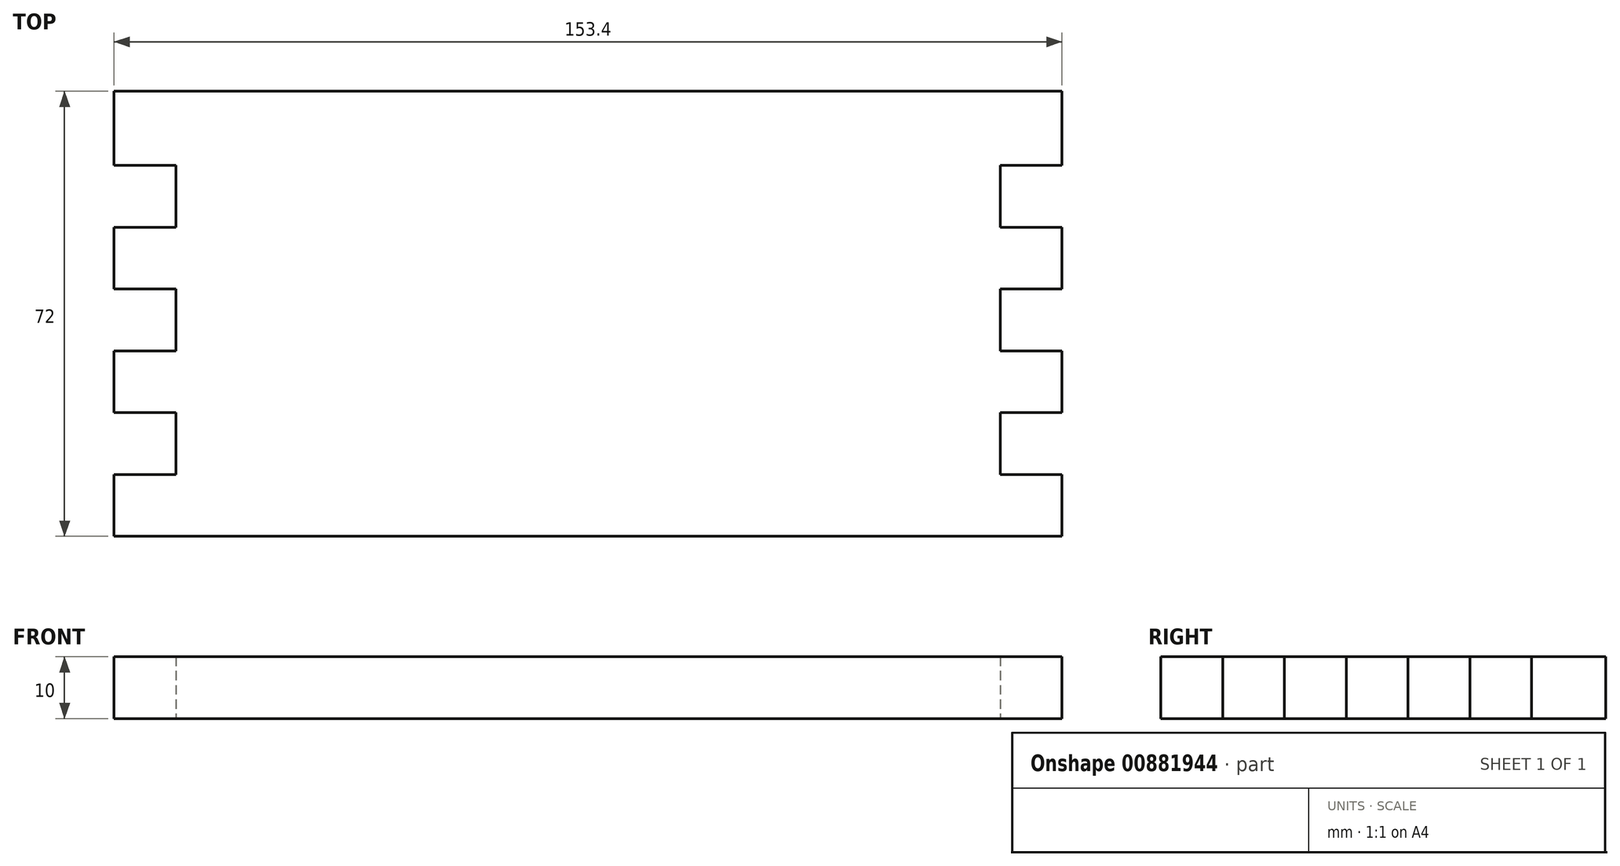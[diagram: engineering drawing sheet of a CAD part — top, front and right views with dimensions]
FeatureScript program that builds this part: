
annotation { "Feature Type Name" : "Feature", "Feature Type Description" : "" }
export const myFeature = defineFeature(function(context is Context, id is Id, definition is map)
    precondition{}
    {
        {
            var Q0;
            Q0=qCreatedBy(makeId("Top.planeOp"),FACE);
            var sketch = newSketch(context, id + "F0", { "sketchPlane" : qUnion([Q0])});
            skLineSegment(sketch, "E0.bottom", {"start": v(-145.63, 36.94) * mm, "end": v(7.77, 36.94) * mm});
            skLineSegment(sketch, "E0.top", {"start": v(-145.63, -33.06) * mm, "end": v(7.77, -33.06) * mm});
            skLineSegment(sketch, "E0.left", {"start": v(-145.63, 36.94) * mm, "end": v(-145.63, -33.06) * mm});
            skLineSegment(sketch, "E0.right", {"start": v(7.77, 36.94) * mm, "end": v(7.77, -33.06) * mm});
            skLineSegment(sketch, "E1.bottom", {"start": v(-145.63, 36.94) * mm, "end": v(-135.63, 36.94) * mm});
            skLineSegment(sketch, "E1.top", {"start": v(-145.63, -33.06) * mm, "end": v(-135.63, -33.06) * mm});
            skLineSegment(sketch, "E1.right", {"start": v(-135.63, 36.94) * mm, "end": v(-135.63, -33.06) * mm});
            skLineSegment(sketch, "E2.bottom", {"start": v(7.77, 36.94) * mm, "end": v(-2.23, 36.94) * mm});
            skLineSegment(sketch, "E2.top", {"start": v(7.77, -33.06) * mm, "end": v(-2.23, -33.06) * mm});
            skLineSegment(sketch, "E2.right", {"start": v(-2.23, 36.94) * mm, "end": v(-2.23, -33.06) * mm});
            skLineSegment(sketch, "E3.left", {"start": v(-145.63, 36.94) * mm, "end": v(-145.63, 26.94) * mm});
            skLineSegment(sketch, "E4.bottom", {"start": v(-2.23, 36.94) * mm, "end": v(7.77, 36.94) * mm});
            skLineSegment(sketch, "E4.top", {"start": v(-2.23, 26.94) * mm, "end": v(7.77, 26.94) * mm});
            skLineSegment(sketch, "E4.left", {"start": v(-2.23, 36.94) * mm, "end": v(-2.23, 26.94) * mm});
            skLineSegment(sketch, "E4.right", {"start": v(7.77, 36.94) * mm, "end": v(7.77, 26.94) * mm});
            skLineSegment(sketch, "E5.MirrorCS", {"start": v(7.77, 16.94) * mm, "end": v(-2.23, 16.94) * mm});
            skLineSegment(sketch, "E6.MirrorCS", {"start": v(-2.23, 6.94) * mm, "end": v(7.77, 6.94) * mm});
            skLineSegment(sketch, "E7.MirrorCS", {"start": v(7.77, -3.06) * mm, "end": v(-2.23, -3.06) * mm});
            skLineSegment(sketch, "E8.MirrorCS", {"start": v(-2.23, -13.06) * mm, "end": v(7.77, -13.06) * mm});
            skLineSegment(sketch, "E9.MirrorCS", {"start": v(7.77, -23.06) * mm, "end": v(-2.23, -23.06) * mm});
            skLineSegment(sketch, "E10.MirrorCS", {"start": v(-2.23, -33.06) * mm, "end": v(7.77, -33.06) * mm});
            skLineSegment(sketch, "E11.top", {"start": v(-145.63, 26.94) * mm, "end": v(-135.63, 26.94) * mm});
            skLineSegment(sketch, "E11.right", {"start": v(-135.63, 36.94) * mm, "end": v(-135.63, 26.94) * mm});
            skLineSegment(sketch, "E12.MirrorCS", {"start": v(-145.63, 16.94) * mm, "end": v(-135.63, 16.94) * mm});
            skLineSegment(sketch, "E13.MirrorCS", {"start": v(-145.63, 6.94) * mm, "end": v(-135.63, 6.94) * mm});
            skLineSegment(sketch, "E14.MirrorCS", {"start": v(-145.63, -3.06) * mm, "end": v(-135.63, -3.06) * mm});
            skLineSegment(sketch, "E15.MirrorCS", {"start": v(-145.63, -13.06) * mm, "end": v(-135.63, -13.06) * mm});
            skLineSegment(sketch, "E16.MirrorCS", {"start": v(-145.63, -23.06) * mm, "end": v(-135.63, -23.06) * mm});
            skLineSegment(sketch, "E17.top", {"start": v(-145.63, 38.94) * mm, "end": v(7.77, 38.94) * mm});
            skLineSegment(sketch, "E17.left", {"start": v(-145.63, 36.94) * mm, "end": v(-145.63, 38.94) * mm});
            skLineSegment(sketch, "E17.right", {"start": v(7.77, 36.94) * mm, "end": v(7.77, 38.94) * mm});
            skSolve(sketch);
        }
        {
            var Q0;
            {var subQ0=sQuery(id+"F0.wireOp",EDGE,"E1.right");var subQ1=sQuery(id+"F0.wireOp",EDGE,"E0.bottom");var subQ2=makeQuery(id+"F0.imprint","INTERSECT",VERTEX,{"derivedFrom":[subQ1,subQ0]});Q0=makeQuery(id+"F0.imprint","IMPRINT",FACE,{"disambiguationData":[TD([[makeQuery(id+"F0.imprint","IMPRINT",EDGE,{"disambiguationData":[TD([[subQ2,-1.0]])],"derivedFrom":subQ1}),-1.0]])]});}
            var Q1;
            {var subQ5=sQuery(id+"F0.wireOp",EDGE,"E11.top");Q1=makeQuery(id+"F0.imprint","IMPRINT",FACE,{"disambiguationData":[TD([[makeQuery(id+"F0.imprint","IMPRINT",EDGE,{"derivedFrom":subQ5}),1.0]])]});}
            var Q2;
            {var subQ0=sQuery(id+"F0.wireOp",EDGE,"E12.MirrorCS");Q2=makeQuery(id+"F0.imprint","IMPRINT",FACE,{"disambiguationData":[TD([[makeQuery(id+"F0.imprint","IMPRINT",EDGE,{"derivedFrom":subQ0}),-1.0]])]});}
            var Q3;
            {var subQ0=sQuery(id+"F0.wireOp",EDGE,"E14.MirrorCS");Q3=makeQuery(id+"F0.imprint","IMPRINT",FACE,{"disambiguationData":[TD([[makeQuery(id+"F0.imprint","IMPRINT",EDGE,{"derivedFrom":subQ0}),-1.0]])]});}
            var Q4;
            {var subQ2=sQuery(id+"F0.wireOp",EDGE,"E16.MirrorCS");Q4=makeQuery(id+"F0.imprint","IMPRINT",FACE,{"disambiguationData":[TD([[makeQuery(id+"F0.imprint","IMPRINT",EDGE,{"derivedFrom":subQ2}),-1.0]])]});}
            var Q5;
            {var subQ5=sQuery(id+"F0.wireOp",EDGE,"f68d17bd-8033-4fb8-93ba-191072b4510d0.MirrorCS");Q5=makeQuery(id+"F0.imprint","IMPRINT",FACE,{"disambiguationData":[TD([[makeQuery(id+"F0.imprint","IMPRINT",EDGE,{"derivedFrom":subQ5}),-1.0]])]});}
            var Q6;
            {var subQ5=sQuery(id+"F0.wireOp",EDGE,"e518cc57-b2af-43e8-af13-6bb7c84993f30.MirrorCS");Q6=makeQuery(id+"F0.imprint","IMPRINT",FACE,{"disambiguationData":[TD([[makeQuery(id+"F0.imprint","IMPRINT",EDGE,{"derivedFrom":subQ5}),1.0]])]});}
            var Q7;
            {var subQ5=sQuery(id+"F0.wireOp",EDGE,"E4.top");Q7=makeQuery(id+"F0.imprint","IMPRINT",FACE,{"disambiguationData":[TD([[makeQuery(id+"F0.imprint","IMPRINT",EDGE,{"derivedFrom":subQ5}),1.0]])]});}
            var Q8;
            {var subQ0=sQuery(id+"F0.wireOp",EDGE,"E5.MirrorCS");Q8=makeQuery(id+"F0.imprint","IMPRINT",FACE,{"disambiguationData":[TD([[makeQuery(id+"F0.imprint","IMPRINT",EDGE,{"derivedFrom":subQ0}),1.0]])]});}
            var Q9;
            {var subQ0=sQuery(id+"F0.wireOp",EDGE,"E7.MirrorCS");Q9=makeQuery(id+"F0.imprint","IMPRINT",FACE,{"disambiguationData":[TD([[makeQuery(id+"F0.imprint","IMPRINT",EDGE,{"derivedFrom":subQ0}),1.0]])]});}
            var Q10;
            {var subQ0=sQuery(id+"F0.wireOp",EDGE,"E9.MirrorCS");Q10=makeQuery(id+"F0.imprint","IMPRINT",FACE,{"disambiguationData":[TD([[makeQuery(id+"F0.imprint","IMPRINT",EDGE,{"derivedFrom":subQ0}),1.0]])]});}
            var Q11;
            Q11=makeQuery(id+"F0.imprint","IMPRINT",FACE,{"disambiguationData":[TD([[makeQuery(id+"F0.imprint","IMPRINT",EDGE,{"derivedFrom":sQuery(id+"F0.wireOp",EDGE,"E17.top")}),-1.0]])]});
            extrude(context, id + "F1", {"entities" : qUnion([Q0, Q1, Q2, Q3, Q4, Q5, Q6, Q7, Q8, Q9, Q10, Q11]), "depth" : 10 * mm, "offsetDistance" : 25 * mm});
        }
    });
